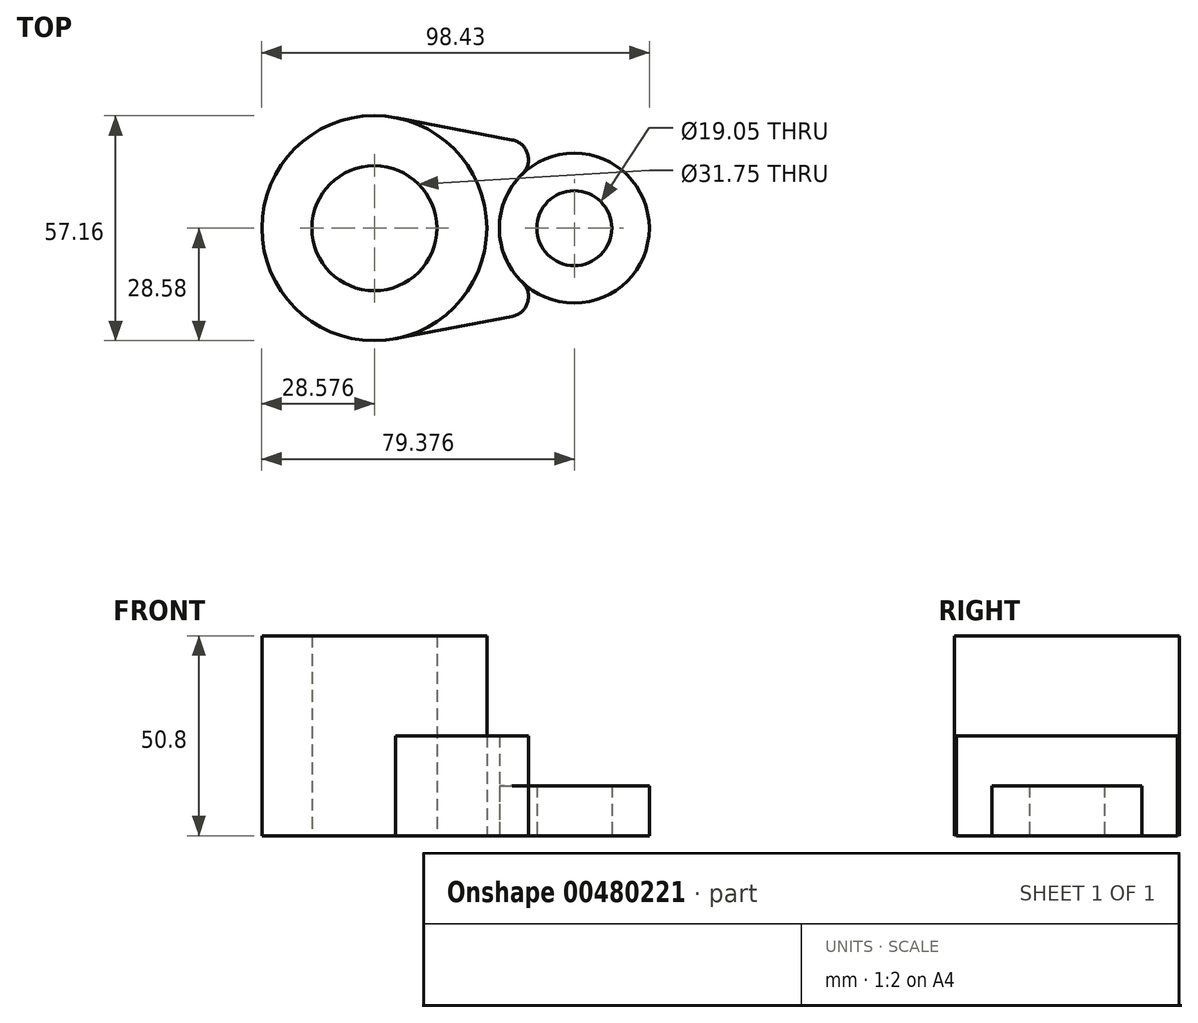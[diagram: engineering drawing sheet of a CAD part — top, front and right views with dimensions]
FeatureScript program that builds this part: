
annotation { "Feature Type Name" : "Feature", "Feature Type Description" : "" }
export const myFeature = defineFeature(function(context is Context, id is Id, definition is map)
    precondition{}
    {
        {
            var Q0;
            Q0=qCreatedBy(makeId("Top.planeOp"),FACE);
            var sketch = newSketch(context, id + "F0", { "sketchPlane" : qUnion([Q0])});
            skCircle(sketch, "E0", {"center": v(-28.6, 0) * mm, "radius": 28.58 * mm});
            skCircle(sketch, "E1", {"center": v(-28.6, 0) * mm, "radius": 15.88 * mm});
            skCircle(sketch, "E2", {"center": v(22.2, 0) * mm, "radius": 19.05 * mm});
            skCircle(sketch, "E3", {"center": v(22.2, 0) * mm, "radius": 9.53 * mm});
            skLineSegment(sketch, "E4", {"start": v(-23.25, 28.07) * mm, "end": v(25.77, 18.71) * mm});
            skLineSegment(sketch, "E5", {"start": v(-23.25, -28.07) * mm, "end": v(25.77, -18.71) * mm});
            skSolve(sketch);
        }
        {
            var Q0;
            Q0=makeQuery(id+"F0.imprint","IMPRINT",FACE,{"disambiguationData":[TD([[makeQuery(id+"F0.imprint","IMPRINT",EDGE,{"derivedFrom":sQuery(id+"F0.wireOp",EDGE,"E1")}),-1.0]])]});
            extrude(context, id + "F1", {"entities" : qUnion([Q0]), "depth" : 25.4 * mm});
        }
        {
            var Q0;
            Q0=makeQuery(id+"F1.opExtrude","CAP_FACE",FACE,{"disambiguationData":[OSD([sQuery(id+"F0.wireOp",EDGE,"E0"),sQuery(id+"F0.wireOp",EDGE,"E1")])],"isStart":false});
            extrude(context, id + "F2", {"entities" : qUnion([Q0]), "operationType" : NewBodyOperationType.ADD, "depth" : 25.4 * mm});
        }
        {
            var Q0;
            Q0=makeQuery(id+"F0.imprint","IMPRINT",FACE,{"disambiguationData":[TD([[makeQuery(id+"F0.imprint","IMPRINT",EDGE,{"derivedFrom":sQuery(id+"F0.wireOp",EDGE,"E3")}),-1.0]])]});
            extrude(context, id + "F3", {"entities" : qUnion([Q0]), "depth" : 12.7 * mm});
        }
        {
            var Q0;
            {var subQ0=sQuery(id+"F0.wireOp",EDGE,"E4");Q0=makeQuery(id+"F0.imprint","IMPRINT",FACE,{"disambiguationData":[TD([[makeQuery(id+"F0.imprint","IMPRINT",EDGE,{"derivedFrom":subQ0}),-1.0]])]});}
            extrude(context, id + "F4", {"entities" : qUnion([Q0]), "depth" : 25.4 * mm});
        }
        {
            var Q0;
            Q0=makeQuery(id+"F4.opExtrude","SWEPT_EDGE",EDGE,{"disambiguationData":[OSD([sQuery(id+"F0.wireOp",EDGE,"E2"),sQuery(id+"F0.wireOp",EDGE,"E5")])]});
            var Q1;
            Q1=makeQuery(id+"F4.opExtrude","SWEPT_EDGE",EDGE,{"disambiguationData":[OSD([sQuery(id+"F0.wireOp",EDGE,"E2"),sQuery(id+"F0.wireOp",EDGE,"E4")])]});
            fillet(context, id + "F5", {"entities" : qUnion([Q0, Q1]), "radius" : 5.08 * mm, "tangentPropagation" : true, "allowEdgeOverflow" : false});
        }
    });
